# Revit family: HVAC-Inffuser-Dadanco-IDL10i
name_source: partatom
category: Mechanical Equipment
revit_build: Autodesk Revit 2015 (Build: 20140903_1530(x64)
units: mm (PartAtom-declared; Revit-internal decimal feet)

## types (1)
- 4' Nominal Length
    Air Inlet Half Length = 0' - 5 1/8"
    Air Inlet Height = 0' - 4 1/32"
    Air Inlet Length = 0' - 10 1/4"
    Air Inlet Radius = 0' - 2 1/32"
    Architectural Design Manual = http://www.dadanco.com
    Assembly Code = D3040100
    Cooling Primary Air Dry Bulb = 0 °F
    Cooling Primary Air Relative Humidity = 0
    Cooling Room Dry Bulb = 0 °F
    Cooling Room Relative Humidity = 0
    Cooling Supply Air Temperature = 0 °F
    Description = Inffuser
    Documentation Link = http://www.dadanco.com
    Grill Material = Metal-Dadanco-Aluminum-Bone White
    Keynote = 23 37 00.A1
    Latent Cooling = 0.0 Btu/h
    Manufacturer = Dadanco
    Model = IDL10I
    Net Unit Cooling Sensible = 0.0 Btu/h
    Nominal Unit Length = 4' - 0"
    Overall Unit Length = 3' - 11 3/4"
    PA = 0 CFM
    PASP = 0.00 in-wg
    Plenum Material = Metal-Dadanco-Steel-Galvanized
    Primary Air Inlet Size = 0' - 8"
    Product Page URL = http://www.dadanco.com
    Revision Date = 04/04/2008
    Supply Air = 0 CFM
    Total Cooling Capacity = 0.0 Btu/h
    Type Comments = 1 way Discharge Internal Entrainment Linear Inffuser
    URL = http://www.dadanco.com
    Unit Height = 0' - 11 3/8"
    Unit Width = 0' - 8 25/32"

## geometry (parser evidence)
native form markers: Sweep x6
no freeform markers — native parametric forms only
